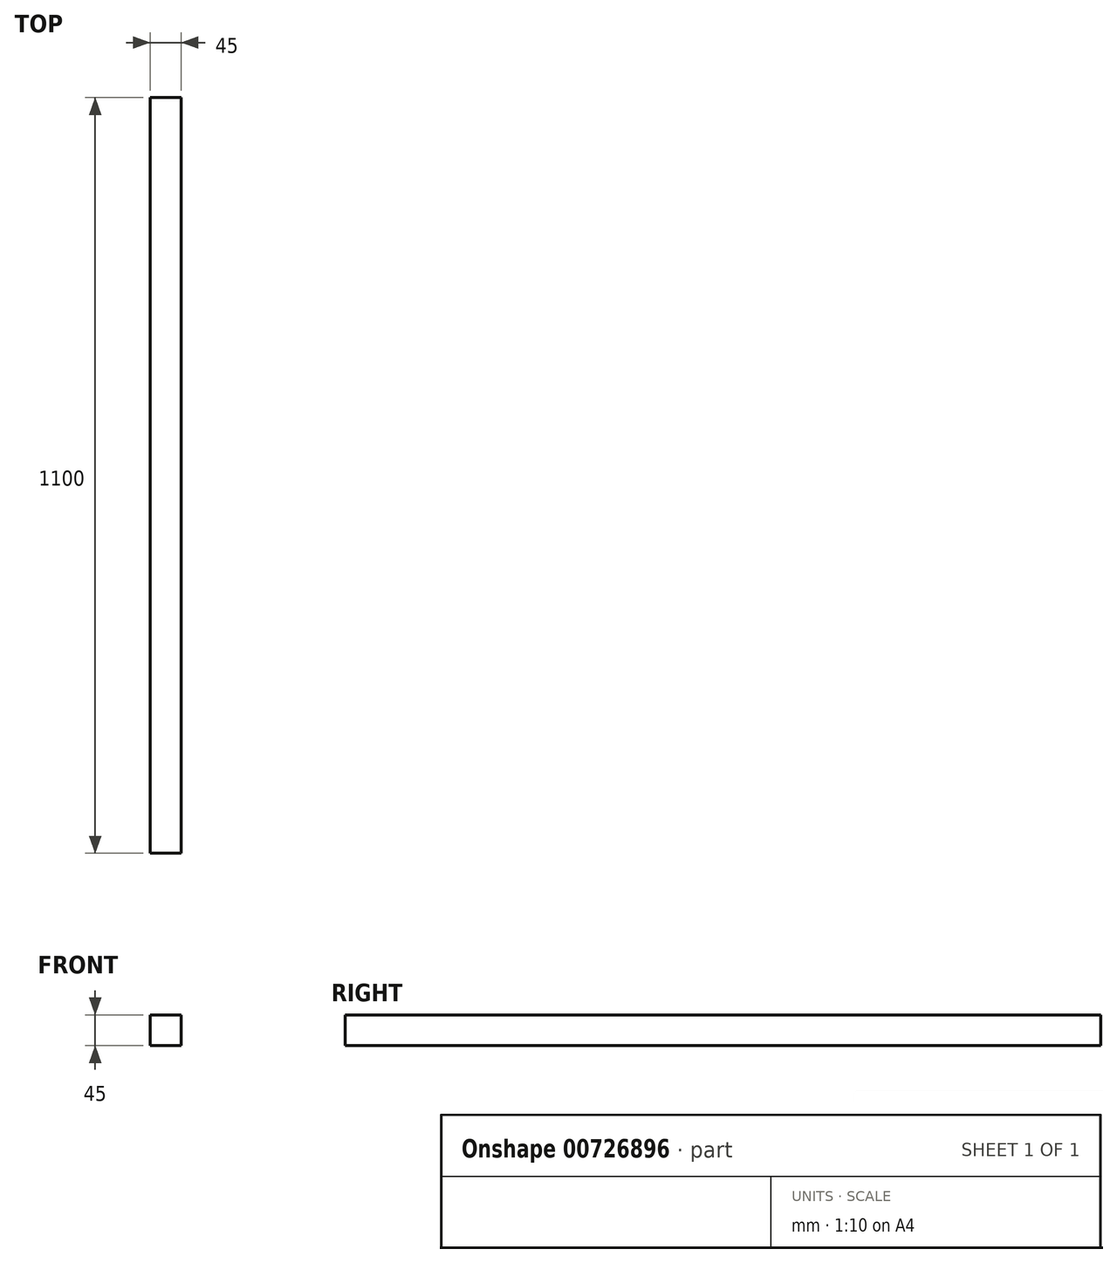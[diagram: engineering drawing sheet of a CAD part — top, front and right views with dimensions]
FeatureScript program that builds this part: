
annotation { "Feature Type Name" : "Feature", "Feature Type Description" : "" }
export const myFeature = defineFeature(function(context is Context, id is Id, definition is map)
    precondition{}
    {
        {
            var Q0;
            Q0=qCreatedBy(makeId("Front.planeOp"),FACE);
            var sketch = newSketch(context, id + "F0", { "sketchPlane" : qUnion([Q0])});
            skLineSegment(sketch, "E0", {"start": v(0, 0) * mm, "end": v(0, 45) * mm});
            skLineSegment(sketch, "E1", {"start": v(0, 45) * mm, "end": v(45, 45) * mm});
            skLineSegment(sketch, "E2", {"start": v(45, 45) * mm, "end": v(45, 0) * mm});
            skLineSegment(sketch, "E3", {"start": v(45, 0) * mm, "end": v(0, 0) * mm});
            skSolve(sketch);
        }
        {
            var Q0;
            Q0 = qSketchRegion(id + "F0", true);
            extrude(context, id + "F1", {"entities" : qUnion([Q0]), "depth" : 1100 * mm, "offsetDistance" : 25 * mm});
        }
    });
